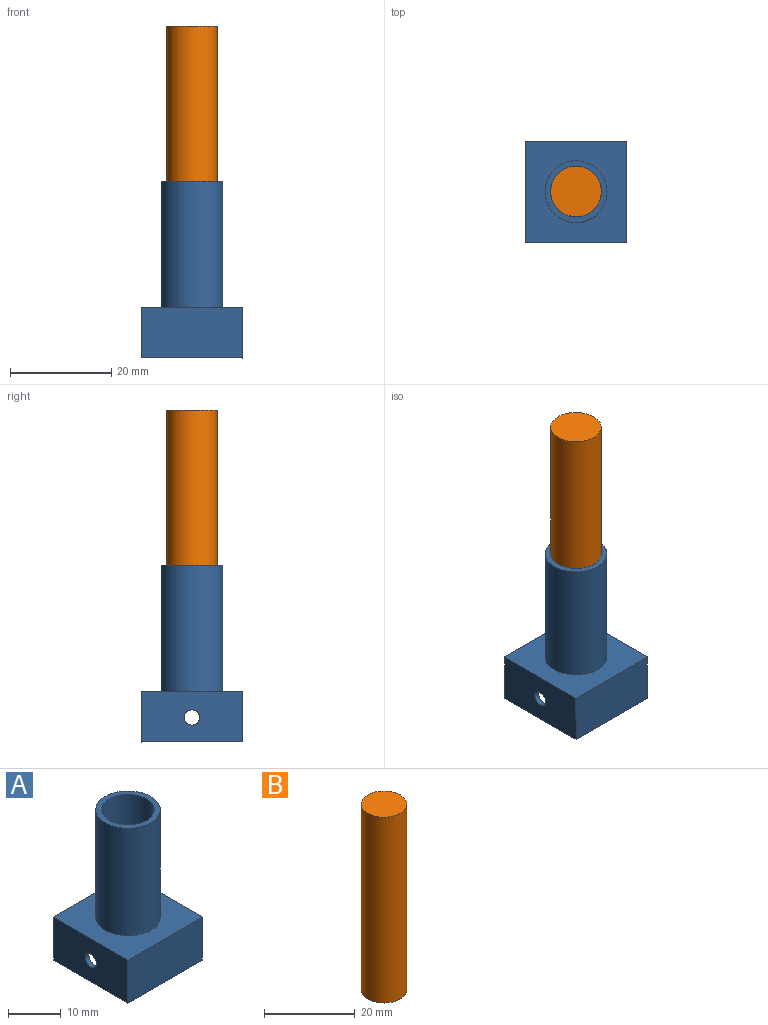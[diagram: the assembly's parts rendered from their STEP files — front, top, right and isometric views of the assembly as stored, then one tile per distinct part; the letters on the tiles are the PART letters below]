
ASSEMBLY  parts=2 mates=1
PART A: 17 faces, bbox 20x20x35 mm
  f0: cylinder r=5mm len=25mm, axis (0,0,-1), area 785.4mm2, adj f2,f8
  f1: cylinder r=6.13mm len=25mm, axis (0,0,-1), area 963.4mm2, adj f2,f3
  f2: plane 12.27x12.27mm, normal (0,0,1), area 39.6mm2, adj f0,f1
  f3: plane 20x20mm, normal (0,0,1), area 281.8mm2, adj f1,f4,f5,f6,f7
  f4: plane 20x10mm, normal (0,-1,0), area 200mm2, adj f3,f5,f7,f13
  f5: plane 20x10mm, normal (-1,0,0), area 192.9mm2, adj f3,f4,f6,f13,f16
  f6: plane 20x10mm, normal (0,1,0), area 200mm2, adj f3,f5,f7,f13
  f7: plane 20x10mm, normal (1,0,0), area 192.9mm2, adj f3,f4,f6,f13,f15
  f8: plane 10x10mm, normal (0,0,1), area 78.5mm2, adj f0
  f9: plane 18x8mm, normal (0,1,0), area 144mm2, adj f10,f12,f13,f14
  f10: plane 18x8mm, normal (1,0,0), area 136.9mm2, adj f9,f11,f13,f14,f16
  f11: plane 18x8mm, normal (0,-1,0), area 144mm2, adj f10,f12,f13,f14
  f12: plane 18x8mm, normal (-1,0,0), area 136.9mm2, adj f9,f11,f13,f14,f15
  f13: plane 20x20mm, normal (0,0,-1), area 76mm2, adj f4,f5,f6,f7,f9,f10,f11,f12
  f14: plane 18x18mm, normal (0,0,-1), area 324mm2, adj f9,f10,f11,f12
  f15: cylinder r=1.5mm len=3mm, axis (1,0,0), area 9.4mm2, adj f7,f12
  f16: cylinder r=1.5mm len=3mm, axis (1,0,0), area 9.4mm2, adj f5,f10
PART B: 3 faces, bbox 10x10x50 mm
  f0: cylinder r=5mm len=50mm, axis (0,0,-1), area 1570.8mm2, adj f1,f2
  f1: plane 10x10mm, normal (0,0,1), area 78.5mm2, adj f0
  f2: plane 10x10mm, normal (0,0,-1), area 78.5mm2, adj f0
PLACE A rot(axis=(-1,0,0.01),0deg) t=(-33.83,6.82,-58.12)mm
PLACE B rot(axis=(1,0,0),180deg) t=(-33.83,6.82,-27.39)mm
MATE slider B.f0 <-> A.f1  axis (0,0,1) through (-33.83,6.82,-2.39)mm
